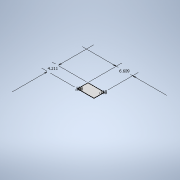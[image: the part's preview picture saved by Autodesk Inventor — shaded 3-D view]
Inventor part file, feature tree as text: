
AUTODESK INVENTOR PART (.ipt)
format: ipt  version: 2020 (Build 240168000, 168)  size: 104,960 bytes
history: native  units: in
note: dims shown in document units (in); Inventor stores cm internally (conversion verified against a paired STEP export)
features: sketch x1, extrude x1, hole x1
ambient origin geometry x8: Origin, YZ Plane, XZ Plane, XY Plane, X Axis, Y Axis, Z Axis, Center Point
bodies: Solid1 (feature_tree)
feature tree (3):
  sketch  "Sketch1"  dims[d0=6.6093in d1=4.2106in d2=0.1678in d3=0.1678in d4=0.1678in d5=0.1678in d6=0.0625in d7=0.0in d8=0.129in d9=0.224in d10=0.225in d11=0.0625in d12=0.5635in d13=0.349in d14=0.8108in]
  extrude  "Extrusion1"  Depth=4.2106in
  hole  "Hole1"  [1 undecoded]
note: 1 required parameter value undecoded (feature->parameter linkage not recoverable at this tier; creation-order binding heuristic only, values carry confidence <= 0.55)
